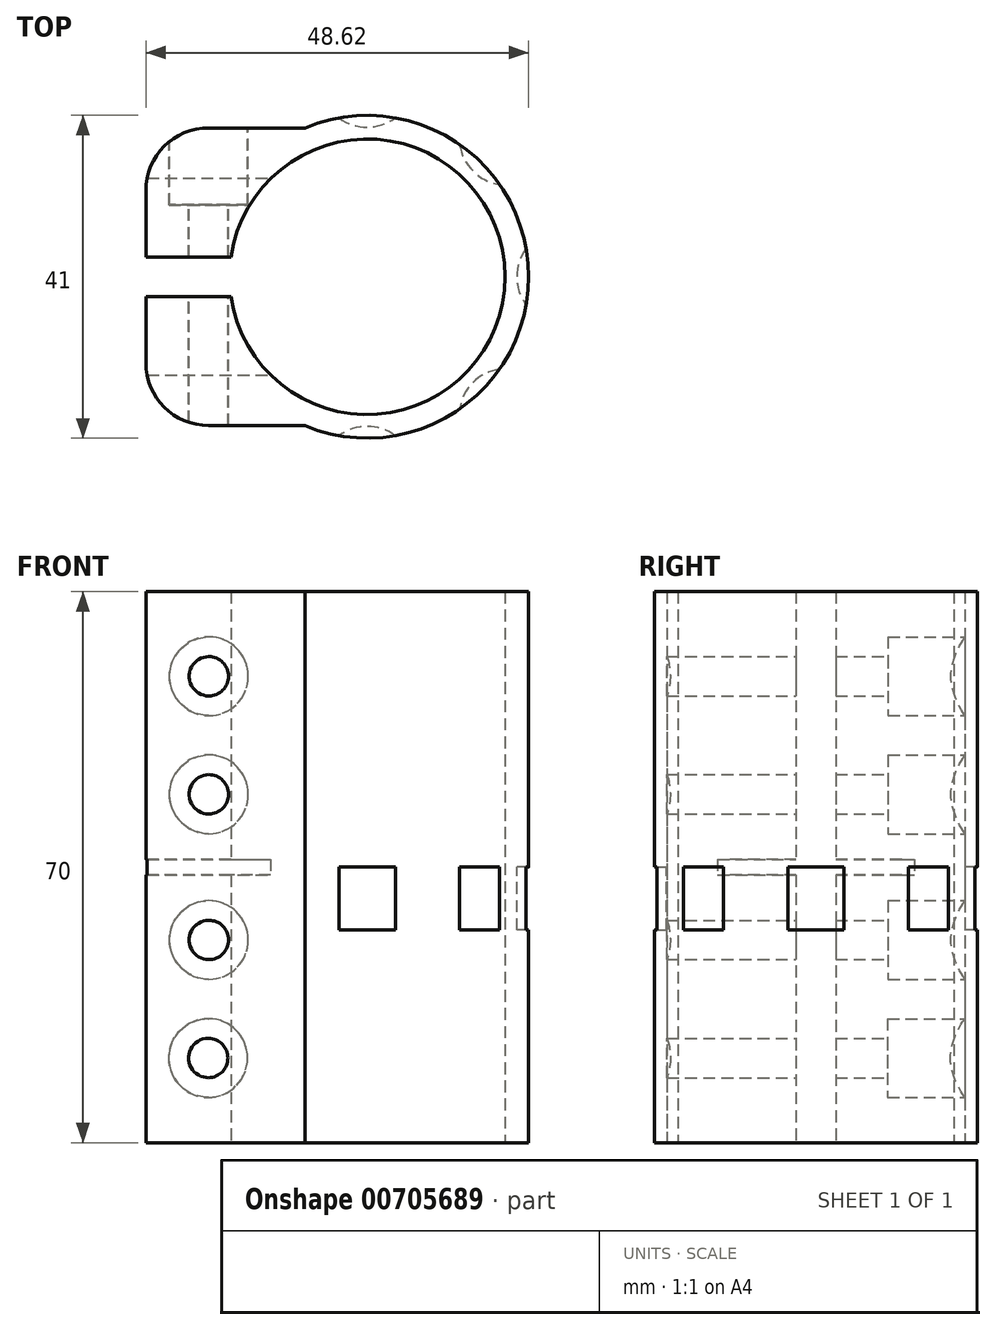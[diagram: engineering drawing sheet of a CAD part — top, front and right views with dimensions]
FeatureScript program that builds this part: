
annotation { "Feature Type Name" : "Feature", "Feature Type Description" : "" }
export const myFeature = defineFeature(function(context is Context, id is Id, definition is map)
    precondition{}
    {
        {
            var Q0;
            Q0=qCreatedBy(makeId("Top.planeOp"),FACE);
            var sketch = newSketch(context, id + "F0", { "sketchPlane" : qUnion([Q0])});
            skArc(sketch, "E0", {"start": v(-17.32, -2.5) * mm, "mid": v(17.5, 0) * mm, "end": v(-17.32, 2.5) * mm});
            skLineSegment(sketch, "E1", {"start": v(-7.92, 18.9) * mm, "end": v(-20.12, 18.9) * mm});
            skLineSegment(sketch, "E2", {"start": v(-28.12, 10.9) * mm, "end": v(-28.12, 2.5) * mm});
            skLineSegment(sketch, "E3", {"start": v(-28.12, 2.5) * mm, "end": v(-17.32, 2.5) * mm});
            skPoint(sketch, "E4.visualSharp", {"position": v(-28.12, 18.9) * mm});
            skArc(sketch, "E4.filletArc", {"start": v(-20.12, 18.9) * mm, "mid": v(-25.78, 16.57) * mm, "end": v(-28.12, 10.9) * mm});
            skLineSegment(sketch, "E5", {"start": v(0, 0) * mm, "end": v(37.25, 0) * mm, "construction": true});
            skLineSegment(sketch, "E6.MirrorCS", {"start": v(-28.12, -10.9) * mm, "end": v(-28.12, -2.5) * mm});
            skLineSegment(sketch, "E7.MirrorCS", {"start": v(-7.92, -18.9) * mm, "end": v(-20.12, -18.9) * mm});
            skLineSegment(sketch, "E8.MirrorCS", {"start": v(-28.12, -2.5) * mm, "end": v(-17.32, -2.5) * mm});
            skArc(sketch, "E9.MirrorCS", {"start": v(-20.12, -18.9) * mm, "mid": v(-25.78, -16.57) * mm, "end": v(-28.12, -10.9) * mm});
            skArc(sketch, "E10.trimOffspring", {"start": v(-7.92, -18.9) * mm, "mid": v(20.5, 0) * mm, "end": v(-7.92, 18.9) * mm});
            skPoint(sketch, "E11.orphan", {"position": v(-17.32, -2.5) * mm});
            skSolve(sketch);
        }
        {
            var Q0;
            Q0 = qSketchRegion(id + "F0", true);
            extrude(context, id + "F1", {"entities" : qUnion([Q0]), "endBound" : BoundingType.SYMMETRIC, "depth" : 70 * mm, "offsetDistance" : 25 * mm});
        }
        {
            var Q0;
            Q0=makeQuery(id+"F1.opExtrude","SWEPT_FACE",FACE,{"disambiguationData":[OSD([sQuery(id+"F0.wireOp",EDGE,"E1")])]});
            var sketch = newSketch(context, id + "F2", { "sketchPlane" : qUnion([Q0])});
            skPoint(sketch, "E12", {"position": v(20.12, 24.25) * mm});
            skPoint(sketch, "E13", {"position": v(20.12, 9.25) * mm});
            skPoint(sketch, "E14", {"position": v(20.12, -9.25) * mm});
            skPoint(sketch, "E15", {"position": v(20.2, -24.25) * mm});
            skSolve(sketch);
        }
        {
            var Q0;
            Q0=sQuery(id+"F2.wireOp",VERTEX,"E12");
            var Q1;
            Q1=sQuery(id+"F2.wireOp",VERTEX,"E13");
            var Q2;
            Q2=sQuery(id+"F2.wireOp",VERTEX,"E14");
            var Q3;
            Q3=sQuery(id+"F2.wireOp",VERTEX,"E15");
            var Q4;
            Q4=makeQuery(id+"F1.opExtrude","SWEPT_BODY",BODY,{"disambiguationData":[OSD([sQuery(id+"F0.wireOp",EDGE,"E0"),sQuery(id+"F0.wireOp",EDGE,"E1"),sQuery(id+"F0.wireOp",EDGE,"E2"),sQuery(id+"F0.wireOp",EDGE,"E3"),sQuery(id+"F0.wireOp",EDGE,"E4.filletArc"),sQuery(id+"F0.wireOp",EDGE,"E6.MirrorCS"),sQuery(id+"F0.wireOp",EDGE,"E7.MirrorCS"),sQuery(id+"F0.wireOp",EDGE,"E8.MirrorCS"),sQuery(id+"F0.wireOp",EDGE,"E9.MirrorCS"),sQuery(id+"F0.wireOp",EDGE,"E10.trimOffspring")])]});
            hole(context, id + "F3", {"style" : HoleStyle.C_BORE, "endStyle" : HoleEndStyle.THROUGH, "holeDiameter" : 5 * mm, "cBoreDiameter" : 10 * mm, "cBoreDepth" : 8 * mm, "majorDiameter" : 5 * mm, "isTappedThrough" : true, "tappedDepth" : 12 * mm, "tapClearance" : 3, "locations" : qUnion([Q0, Q1, Q2, Q3]), "scope" : qUnion([Q4])});
        }
        {
            var Q0;
            Q0=qCreatedBy(makeId("Front.planeOp"),FACE);
            var sketch = newSketch(context, id + "F4", { "sketchPlane" : qUnion([Q0])});
            skLineSegment(sketch, "E16.bottom", {"start": v(-28.12, -1) * mm, "end": v(-5.72, -1) * mm});
            skLineSegment(sketch, "E16.top", {"start": v(-28.12, 1) * mm, "end": v(-5.72, 1) * mm});
            skLineSegment(sketch, "E16.left", {"start": v(-28.12, -1) * mm, "end": v(-28.12, 1) * mm});
            skLineSegment(sketch, "E16.right", {"start": v(-5.72, -1) * mm, "end": v(-5.72, 1) * mm});
            skSolve(sketch);
        }
        {
            var Q0;
            Q0 = qSketchRegion(id + "F4", true);
            extrude(context, id + "F5", {"entities" : qUnion([Q0]), "operationType" : NewBodyOperationType.REMOVE, "endBound" : BoundingType.SYMMETRIC, "oppositeDirection" : true, "depth" : 25 * mm, "offsetDistance" : 25 * mm});
        }
        {
            var Q0;
            Q0=qCreatedBy(makeId("Top.planeOp"),FACE);
            var sketch = newSketch(context, id + "F6", { "sketchPlane" : qUnion([Q0])});
            skCircle(sketch, "E17", {"center": v(0, -25) * mm, "radius": 6 * mm});
            skCircle(sketch, "E18.1.0", {"center": v(17.68, -17.68) * mm, "radius": 6 * mm});
            skCircle(sketch, "E18.2.0", {"center": v(25, 0) * mm, "radius": 6 * mm});
            skCircle(sketch, "E18.3.0", {"center": v(17.68, 17.68) * mm, "radius": 6 * mm});
            skCircle(sketch, "E18.4.0", {"center": v(0, 25) * mm, "radius": 6 * mm});
            skPoint(sketch, "E18.center", {"position": v(0, 0) * mm});
            skLineSegment(sketch, "E18.anchor1", {"start": v(0, 0) * mm, "end": v(0, -25) * mm, "construction": true});
            skLineSegment(sketch, "E18.anchor2", {"start": v(0, 0) * mm, "end": v(0, 25) * mm, "construction": true});
            skSolve(sketch);
        }
        {
            var Q0;
            Q0 = qSketchRegion(id + "F6", true);
            extrude(context, id + "F7", {"entities" : qUnion([Q0]), "operationType" : NewBodyOperationType.REMOVE, "oppositeDirection" : true, "depth" : 8 * mm, "offsetDistance" : 25 * mm});
        }
    });
